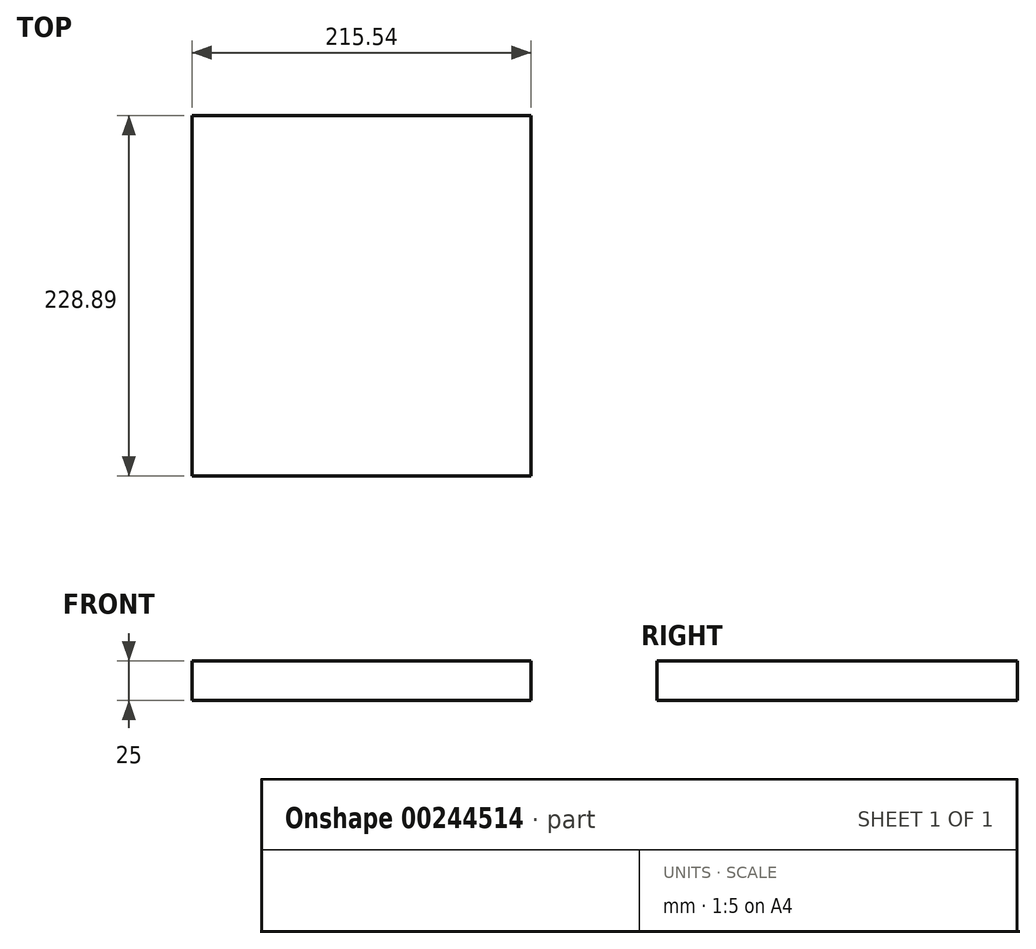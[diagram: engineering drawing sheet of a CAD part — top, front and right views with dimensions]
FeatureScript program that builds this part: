
annotation { "Feature Type Name" : "Feature", "Feature Type Description" : "" }
export const myFeature = defineFeature(function(context is Context, id is Id, definition is map)
    precondition{}
    {
        {
            var Q0;
            Q0=qCreatedBy(makeId("Top.planeOp"),FACE);
            var sketch = newSketch(context, id + "F0", { "sketchPlane" : qUnion([Q0])});
            skLineSegment(sketch, "E0.bottom", {"start": v(-108.12, 98.64) * mm, "end": v(107.42, 98.64) * mm});
            skLineSegment(sketch, "E0.top", {"start": v(-108.12, -130.25) * mm, "end": v(107.42, -130.25) * mm});
            skLineSegment(sketch, "E0.left", {"start": v(-108.12, 98.64) * mm, "end": v(-108.12, -130.25) * mm});
            skLineSegment(sketch, "E0.right", {"start": v(107.42, 98.64) * mm, "end": v(107.42, -130.25) * mm});
            skSolve(sketch);
        }
        {
            var Q0;
            Q0 = qSketchRegion(id + "F0", true);
            extrude(context, id + "F1", {"entities" : qUnion([Q0]), "oppositeDirection" : true, "depth" : 25 * mm});
        }
    });
